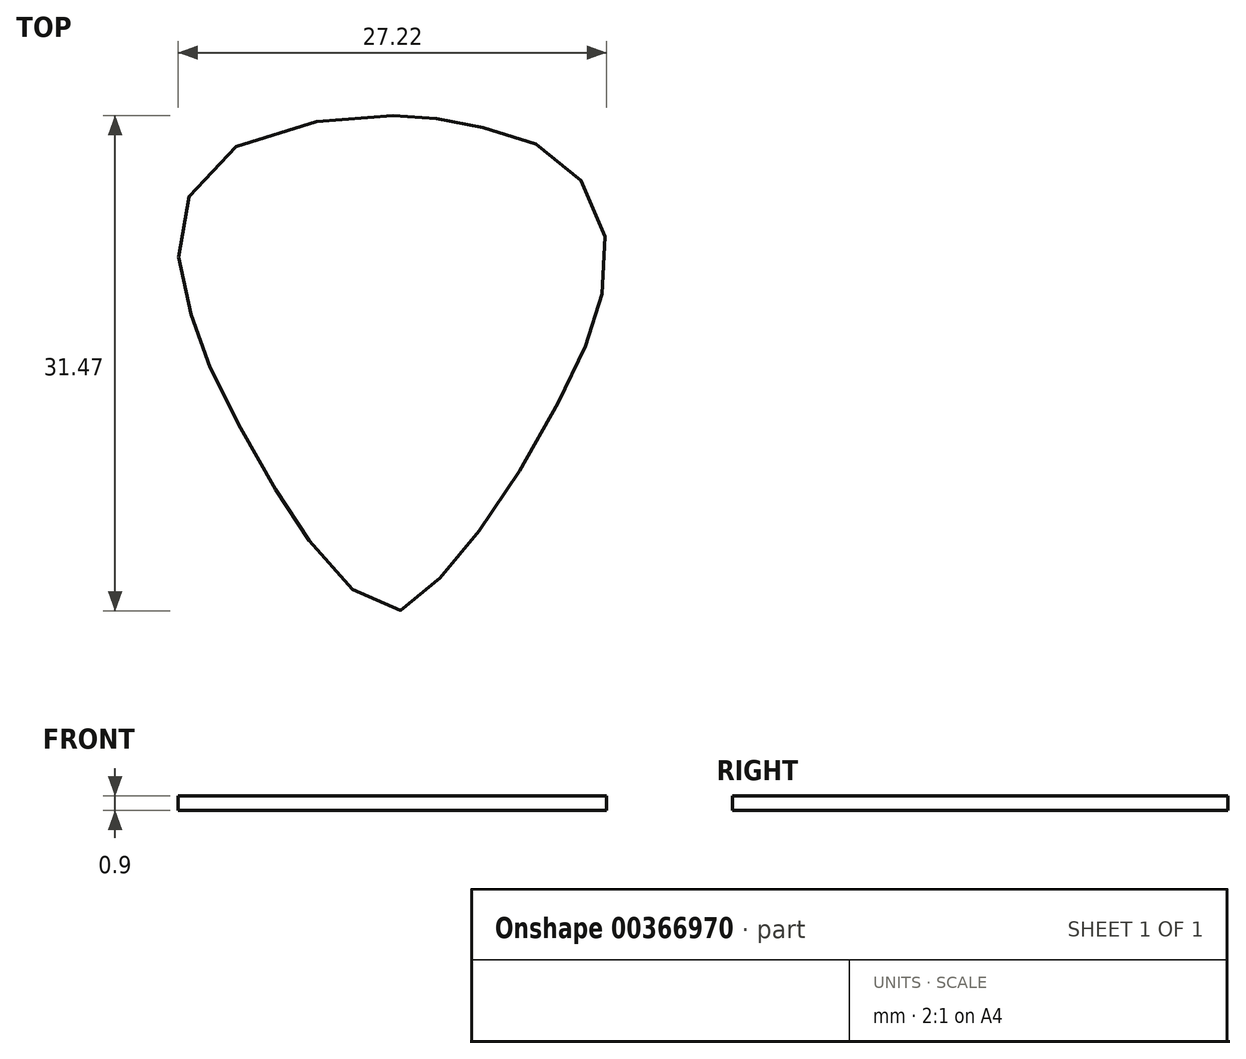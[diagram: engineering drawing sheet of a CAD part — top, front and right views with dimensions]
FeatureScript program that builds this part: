
annotation { "Feature Type Name" : "Feature", "Feature Type Description" : "" }
export const myFeature = defineFeature(function(context is Context, id is Id, definition is map)
    precondition{}
    {
        {
            var Q0;
            Q0=qCreatedBy(makeId("Top.planeOp"),FACE);
            var sketch = newSketch(context, id + "F0", { "sketchPlane" : qUnion([Q0])});
            skPoint(sketch, "E0.19.internal.snap0", {"position": v(0, -16.18) * mm});
            skFitSpline(sketch, "E1", {"points": [v(0, 16.93) * mm, v(2.82, 16.73) * mm, v(6.36, 16.01) * mm, v(10.69, 14.12) * mm, v(13.44, 9.42) * mm, v(12.98, 4.52) * mm, v(11.15, 0) * mm, v(6.77, -7.62) * mm, v(2.97, -12.45) * mm, v(0, -14.54) * mm, v(-4.3, -11.34) * mm, v(-7.58, -6.64) * mm, v(-11.19, 0) * mm, v(-12.96, 4.66) * mm, v(-13.55, 9.95) * mm, v(-9.62, 15.17) * mm, v(0, 16.93) * mm]});
            skSolve(sketch);
        }
        {
            var Q0;
            Q0 = qSketchRegion(id + "F0", true);
            extrude(context, id + "F1", {"entities" : qUnion([Q0]), "depth" : 0.9 * mm});
        }
    });
